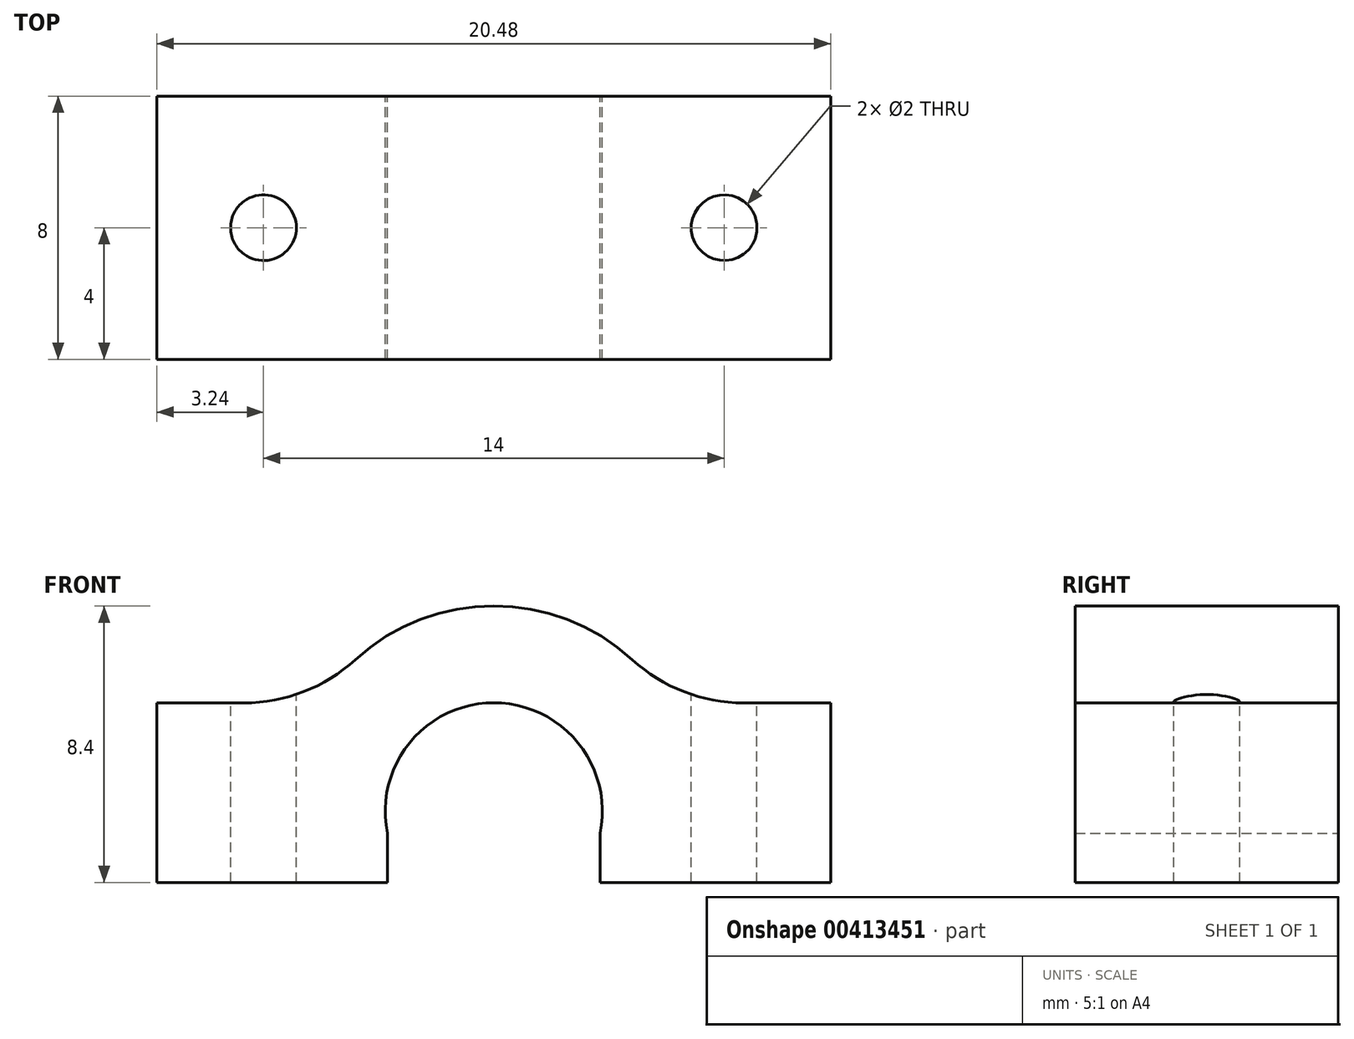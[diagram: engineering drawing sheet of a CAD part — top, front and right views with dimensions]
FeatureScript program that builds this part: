
annotation { "Feature Type Name" : "Feature", "Feature Type Description" : "" }
export const myFeature = defineFeature(function(context is Context, id is Id, definition is map)
    precondition{}
    {
        {
            var Q0;
            Q0=qCreatedBy(makeId("Front.planeOp"),FACE);
            var sketch = newSketch(context, id + "F0", { "sketchPlane" : qUnion([Q0])});
            skArc(sketch, "E0", {"start": v(3.23, -0.66) * mm, "mid": v(0, 3.3) * mm, "end": v(-3.23, -0.66) * mm});
            skArc(sketch, "E1", {"start": v(4.21, 4.6) * mm, "mid": v(0, 6.24) * mm, "end": v(-4.21, 4.6) * mm});
            skLineSegment(sketch, "E2.bottom", {"start": v(-10.24, -0.66) * mm, "end": v(-3.23, -0.66) * mm});
            skLineSegment(sketch, "E2.top", {"start": v(-10.24, 3.3) * mm, "end": v(-7.59, 3.3) * mm});
            skLineSegment(sketch, "E2.left", {"start": v(-10.24, -0.66) * mm, "end": v(-10.24, 3.3) * mm});
            skLineSegment(sketch, "E2.right", {"start": v(10.24, -0.66) * mm, "end": v(10.24, 3.3) * mm});
            skLineSegment(sketch, "E3.trimOffspring", {"start": v(7.59, 3.3) * mm, "end": v(10.24, 3.3) * mm});
            skLineSegment(sketch, "E4.trimOffspring", {"start": v(-0.15, 3.3) * mm, "end": v(0.15, 3.3) * mm});
            skLineSegment(sketch, "E5.trimOffspring", {"start": v(3.23, -0.66) * mm, "end": v(10.24, -0.66) * mm});
            skPoint(sketch, "E6.visualSharp", {"position": v(-5.3, 3.3) * mm});
            skArc(sketch, "E6.filletArc", {"start": v(-7.59, 3.3) * mm, "mid": v(-5.78, 3.64) * mm, "end": v(-4.21, 4.6) * mm});
            skPoint(sketch, "E7.visualSharp", {"position": v(5.3, 3.3) * mm});
            skArc(sketch, "E7.filletArc", {"start": v(4.21, 4.6) * mm, "mid": v(5.78, 3.64) * mm, "end": v(7.59, 3.3) * mm});
            skSolve(sketch);
        }
        {
            var Q0;
            Q0=makeQuery(id+"F0.imprint","IMPRINT",FACE,{"disambiguationData":[TD([[makeQuery(id+"F0.imprint","IMPRINT",EDGE,{"derivedFrom":sQuery(id+"F0.wireOp",EDGE,"E1")}),1.0]])]});
            extrude(context, id + "F1", {"entities" : qUnion([Q0]), "depth" : 8 * mm});
        }
        {
            var Q0;
            Q0=qCreatedBy(makeId("Top.planeOp"),FACE);
            var sketch = newSketch(context, id + "F2", { "sketchPlane" : qUnion([Q0])});
            skLineSegment(sketch, "E8", {"start": v(-18.6, -4) * mm, "end": v(17.66, -4) * mm});
            skLineSegment(sketch, "E9", {"start": v(-7, -8.96) * mm, "end": v(-7, 1.39) * mm});
            skCircle(sketch, "E10", {"center": v(-7, -4) * mm, "radius": 1 * mm});
            skLineSegment(sketch, "E11", {"start": v(7, -9.27) * mm, "end": v(7, 1.61) * mm});
            skCircle(sketch, "E12", {"center": v(7, -4) * mm, "radius": 1 * mm});
            skSolve(sketch);
        }
        {
            var Q0;
            Q0=sQuery(id+"F2.wireOp",VERTEX,"E10.center");
            var Q1;
            Q1=sQuery(id+"F2.wireOp",VERTEX,"E12.center");
            var Q2;
            Q2=makeQuery(id+"F1.opExtrude","SWEPT_BODY",BODY,{"disambiguationData":[OSD([sQuery(id+"F0.wireOp",EDGE,"E0"),sQuery(id+"F0.wireOp",EDGE,"E1"),sQuery(id+"F0.wireOp",EDGE,"E2.bottom"),sQuery(id+"F0.wireOp",EDGE,"E2.top"),sQuery(id+"F0.wireOp",EDGE,"E2.left"),sQuery(id+"F0.wireOp",EDGE,"E2.right"),sQuery(id+"F0.wireOp",EDGE,"E3.trimOffspring"),sQuery(id+"F0.wireOp",EDGE,"E5.trimOffspring"),sQuery(id+"F0.wireOp",EDGE,"E6.filletArc"),sQuery(id+"F0.wireOp",EDGE,"E7.filletArc")])]});
            hole(context, id + "F3", {"style" : HoleStyle.SIMPLE, "endStyle" : HoleEndStyle.THROUGH, "holeDiameter" : 2 * mm, "isTappedThrough" : true, "tappedDepth" : 12 * mm, "tapClearance" : 3, "startFromSketch" : true, "locations" : qUnion([Q0, Q1]), "scope" : qUnion([Q2])});
        }
        {
            var Q0;
            Q0=sQuery(id+"F2.wireOp",VERTEX,"E10.center");
            var Q1;
            Q1=sQuery(id+"F2.wireOp",VERTEX,"E12.center");
            var Q2;
            Q2=makeQuery(id+"F1.opExtrude","SWEPT_BODY",BODY,{"disambiguationData":[OSD([sQuery(id+"F0.wireOp",EDGE,"E0"),sQuery(id+"F0.wireOp",EDGE,"E1"),sQuery(id+"F0.wireOp",EDGE,"E2.bottom"),sQuery(id+"F0.wireOp",EDGE,"E2.top"),sQuery(id+"F0.wireOp",EDGE,"E2.left"),sQuery(id+"F0.wireOp",EDGE,"E2.right"),sQuery(id+"F0.wireOp",EDGE,"E3.trimOffspring"),sQuery(id+"F0.wireOp",EDGE,"E5.trimOffspring"),sQuery(id+"F0.wireOp",EDGE,"E6.filletArc"),sQuery(id+"F0.wireOp",EDGE,"E7.filletArc")])]});
            hole(context, id + "F4", {"style" : HoleStyle.SIMPLE, "endStyle" : HoleEndStyle.THROUGH, "oppositeDirection" : true, "holeDiameter" : 2 * mm, "isTappedThrough" : true, "tappedDepth" : 12 * mm, "tapClearance" : 3, "startFromSketch" : true, "locations" : qUnion([Q0, Q1]), "scope" : qUnion([Q2])});
        }
        {
            var Q0;
            Q0=makeQuery(id+"F1.opExtrude","SWEPT_FACE",FACE,{"disambiguationData":[OSD([sQuery(id+"F0.wireOp",EDGE,"E5.trimOffspring")])]});
            var Q1;
            Q1=makeQuery(id+"F1.opExtrude","SWEPT_FACE",FACE,{"disambiguationData":[OSD([sQuery(id+"F0.wireOp",EDGE,"E2.bottom")])]});
            extrude(context, id + "F5", {"entities" : qUnion([Q0, Q1]), "operationType" : NewBodyOperationType.ADD, "depth" : 1.5 * mm});
        }
    });
